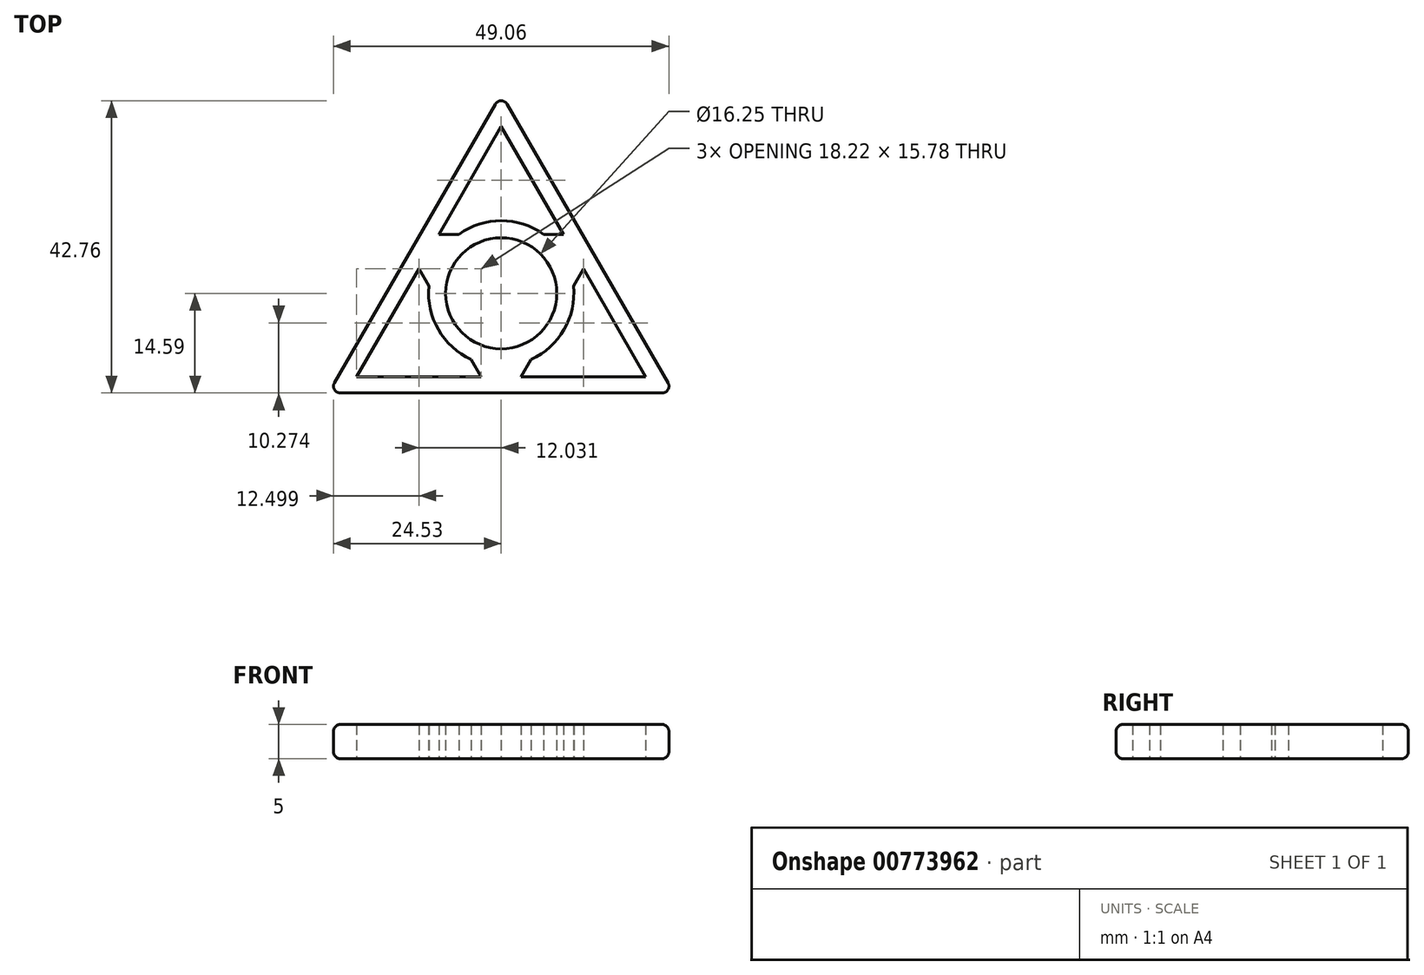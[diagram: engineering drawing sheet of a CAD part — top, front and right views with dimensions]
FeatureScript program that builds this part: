
annotation { "Feature Type Name" : "Feature", "Feature Type Description" : "" }
export const myFeature = defineFeature(function(context is Context, id is Id, definition is map)
    precondition{}
    {
        {
            var Q0;
            Q0=qCreatedBy(makeId("Top.planeOp"),FACE);
            var sketch = newSketch(context, id + "F0", { "sketchPlane" : qUnion([Q0])});
            skCircle(sketch, "E0", {"center": v(0, 0) * mm, "radius": 8.12 * mm});
            skPoint(sketch, "E1.0.midPoint", {"position": v(-15.75, 9.1) * mm});
            skPoint(sketch, "E2.0.midPoint", {"position": v(-4.68, 21.35) * mm});
            skPoint(sketch, "E2.2.end.orphan", {"position": v(-9.43, 13.25) * mm});
            skPoint(sketch, "E2.0.end.orphan", {"position": v(0.07, 29.45) * mm});
            skLineSegment(sketch, "E3.0", {"start": v(-25.26, -14.59) * mm, "end": v(0, 29.17) * mm});
            skLineSegment(sketch, "E3.1", {"start": v(25.26, -14.59) * mm, "end": v(-25.26, -14.59) * mm});
            skLineSegment(sketch, "E3.2", {"start": v(0, 29.17) * mm, "end": v(25.26, -14.59) * mm});
            skPoint(sketch, "E1.1.start.orphan", {"position": v(0, 36.37) * mm});
            skPoint(sketch, "E1.2.start.orphan", {"position": v(31.5, -18.19) * mm});
            skPoint(sketch, "E1.0.start.orphan", {"position": v(-31.5, -18.19) * mm});
            skLineSegment(sketch, "E4", {"start": v(0, 29.17) * mm, "end": v(0, -17.04) * mm, "construction": true});
            skPoint(sketch, "E5.0.midPoint", {"position": v(0, 7.43) * mm});
            skLineSegment(sketch, "E6.0", {"start": v(-9.11, 8.63) * mm, "end": v(0, 24.41) * mm});
            skLineSegment(sketch, "E6.1", {"start": v(9.11, 8.63) * mm, "end": v(-9.11, 8.63) * mm});
            skLineSegment(sketch, "E6.2", {"start": v(0, 24.41) * mm, "end": v(9.11, 8.63) * mm});
            skPoint(sketch, "E7.orphan", {"position": v(0, 26.81) * mm});
            skPoint(sketch, "E8.orphan", {"position": v(-11.19, 7.43) * mm});
            skPoint(sketch, "E5.2.end.orphan", {"position": v(11.19, 7.43) * mm});
            skCircle(sketch, "E9.0", {"center": v(0, 0) * mm, "radius": 10.62 * mm});
            skLineSegment(sketch, "E10.1.0", {"start": v(-2.92, -12.2) * mm, "end": v(-21.14, -12.2) * mm});
            skLineSegment(sketch, "E10.1.1", {"start": v(-21.14, -12.2) * mm, "end": v(-12.03, 3.57) * mm});
            skLineSegment(sketch, "E10.1.2", {"start": v(-12.03, 3.57) * mm, "end": v(-2.92, -12.2) * mm});
            skLineSegment(sketch, "E10.2.0", {"start": v(12.03, 3.57) * mm, "end": v(21.14, -12.2) * mm});
            skLineSegment(sketch, "E10.2.1", {"start": v(21.14, -12.2) * mm, "end": v(2.92, -12.2) * mm});
            skLineSegment(sketch, "E10.2.2", {"start": v(2.92, -12.2) * mm, "end": v(12.03, 3.57) * mm});
            skSolve(sketch);
        }
        {
            var Q0;
            Q0=qSketchRegion(id+"F0",true);
            var Q1;
            Q1=makeQuery(id+"F0.imprint","IMPRINT",FACE,{"disambiguationData":[TD([[makeQuery(id+"F0.imprint","IMPRINT",EDGE,{"derivedFrom":sQuery(id+"F0.wireOp",EDGE,"E0")}),-1.0]])]});
            var Q2;
            {var subQ0=sQuery(id+"F0.wireOp",EDGE,"E9.0");var subQ1=sQuery(id+"F0.wireOp",EDGE,"E10.1.2");var subQ2=makeQuery(id+"F0.imprint","INTERSECT",VERTEX,{"disambiguationData":[OD(0.0)],"derivedFrom":[subQ1,subQ0]});Q2=makeQuery(id+"F0.imprint","IMPRINT",FACE,{"disambiguationData":[TD([[makeQuery(id+"F0.imprint","IMPRINT",EDGE,{"disambiguationData":[TD([[subQ2,-1.0]])],"derivedFrom":subQ1}),-1.0]])]});}
            var Q3;
            {var subQ0=sQuery(id+"F0.wireOp",EDGE,"E9.0");var subQ1=sQuery(id+"F0.wireOp",EDGE,"E10.2.2");var subQ2=makeQuery(id+"F0.imprint","INTERSECT",VERTEX,{"disambiguationData":[OD(0.0)],"derivedFrom":[subQ1,subQ0]});Q3=makeQuery(id+"F0.imprint","IMPRINT",FACE,{"disambiguationData":[TD([[makeQuery(id+"F0.imprint","IMPRINT",EDGE,{"disambiguationData":[TD([[subQ2,-1.0]])],"derivedFrom":subQ1}),-1.0]])]});}
            var Q4;
            {var subQ0=sQuery(id+"F0.wireOp",EDGE,"E9.0");var subQ1=sQuery(id+"F0.wireOp",EDGE,"E6.1");var subQ2=makeQuery(id+"F0.imprint","INTERSECT",VERTEX,{"disambiguationData":[OD(0.0)],"derivedFrom":[subQ1,subQ0]});Q4=makeQuery(id+"F0.imprint","IMPRINT",FACE,{"disambiguationData":[TD([[makeQuery(id+"F0.imprint","IMPRINT",EDGE,{"disambiguationData":[TD([[subQ2,-1.0]])],"derivedFrom":subQ1}),-1.0]])]});}
            extrude(context, id + "F1", {"entities" : qUnion([Q0, Q1, Q2, Q3, Q4]), "depth" : 5 * mm, "offsetDistance" : 25 * mm});
        }
        {
            var Q0;
            Q0=makeQuery(id+"F1.opExtrude","CAP_EDGE",EDGE,{"disambiguationData":[OSD([sQuery(id+"F0.wireOp",EDGE,"E3.2")])],"isStart":true});
            var Q1;
            Q1=makeQuery(id+"F1.opExtrude","CAP_EDGE",EDGE,{"disambiguationData":[OSD([sQuery(id+"F0.wireOp",EDGE,"E3.0")])],"isStart":true});
            var Q2;
            Q2=makeQuery(id+"F1.opExtrude","CAP_EDGE",EDGE,{"disambiguationData":[OSD([sQuery(id+"F0.wireOp",EDGE,"E3.1")])],"isStart":true});
            var Q3;
            Q3=makeQuery(id+"F1.opExtrude","CAP_EDGE",EDGE,{"disambiguationData":[OSD([sQuery(id+"F0.wireOp",EDGE,"E3.0")])],"isStart":false});
            var Q4;
            Q4=makeQuery(id+"F1.opExtrude","CAP_EDGE",EDGE,{"disambiguationData":[OSD([sQuery(id+"F0.wireOp",EDGE,"E3.2")])],"isStart":false});
            var Q5;
            Q5=makeQuery(id+"F1.opExtrude","CAP_EDGE",EDGE,{"disambiguationData":[OSD([sQuery(id+"F0.wireOp",EDGE,"E3.1")])],"isStart":false});
            var Q6;
            Q6=makeQuery(id+"F1.opExtrude","SWEPT_EDGE",EDGE,{"disambiguationData":[OSD([sQuery(id+"F0.wireOp",EDGE,"E3.0"),sQuery(id+"F0.wireOp",EDGE,"E3.1")])]});
            var Q7;
            Q7=makeQuery(id+"F1.opExtrude","SWEPT_EDGE",EDGE,{"disambiguationData":[OSD([sQuery(id+"F0.wireOp",EDGE,"E3.0"),sQuery(id+"F0.wireOp",EDGE,"E3.2")])]});
            var Q8;
            Q8=makeQuery(id+"F1.opExtrude","SWEPT_EDGE",EDGE,{"disambiguationData":[OSD([sQuery(id+"F0.wireOp",EDGE,"E3.1"),sQuery(id+"F0.wireOp",EDGE,"E3.2")])]});
            fillet(context, id + "F2", {"entities" : qUnion([Q0, Q1, Q2, Q3, Q4, Q5, Q6, Q7, Q8]), "radius" : 1 * mm, "tangentPropagation" : true, "allowEdgeOverflow" : false});
        }
    });
